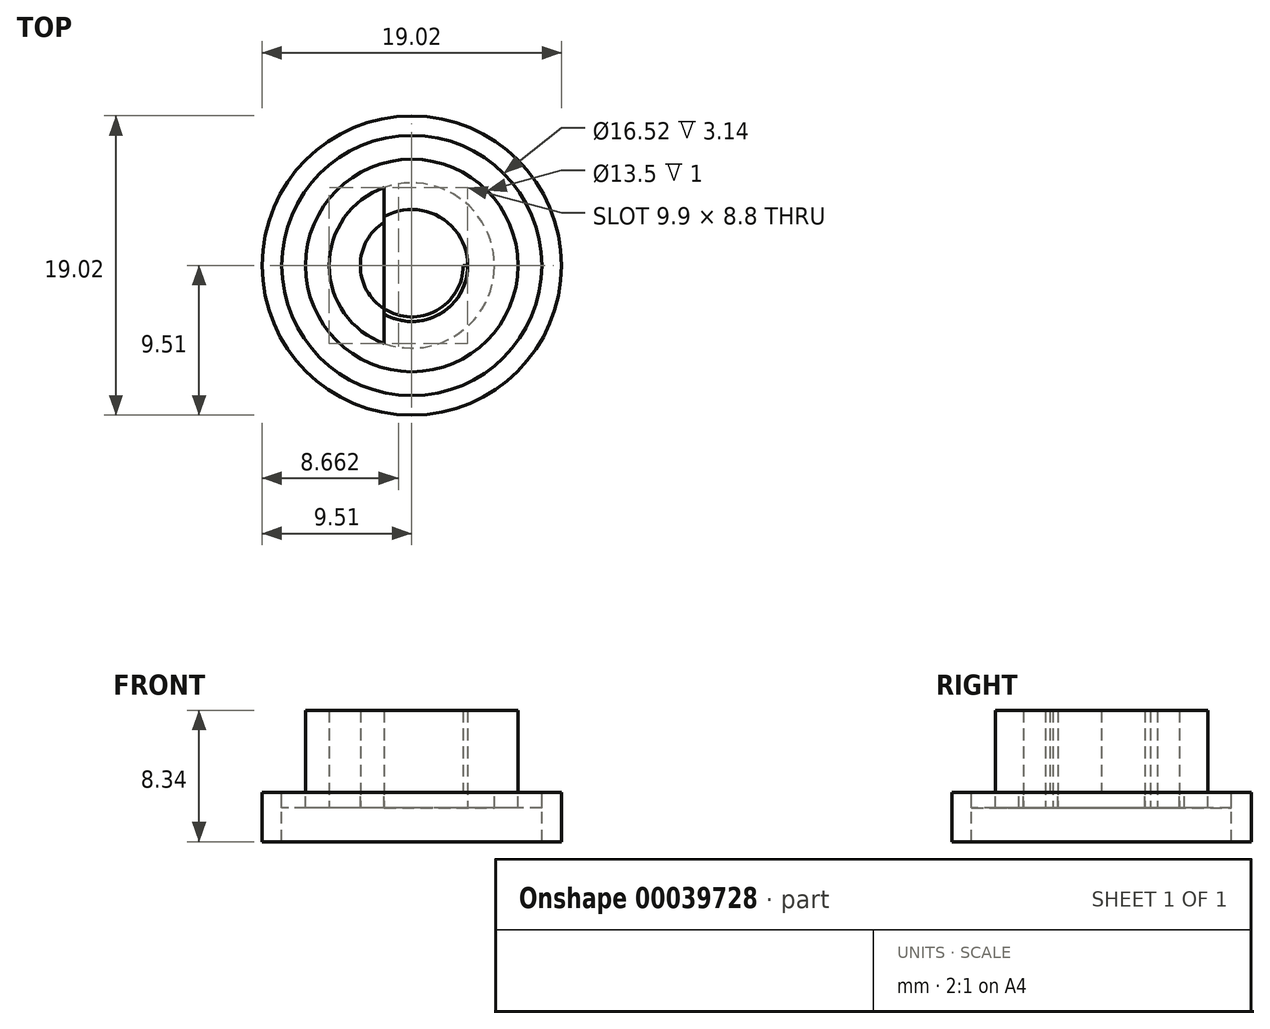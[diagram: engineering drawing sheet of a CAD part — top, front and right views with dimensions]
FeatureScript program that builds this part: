
annotation { "Feature Type Name" : "Feature", "Feature Type Description" : "" }
export const myFeature = defineFeature(function(context is Context, id is Id, definition is map)
    precondition{}
    {
        {
            var Q0;
            Q0=qCreatedBy(makeId("Top.planeOp"),FACE);
            var sketch = newSketch(context, id + "F0", { "sketchPlane" : qUnion([Q0])});
            skCircle(sketch, "E0", {"center": v(0, 0) * mm, "radius": 3.56 * mm});
            skCircle(sketch, "E1", {"center": v(0, 0) * mm, "radius": 5.25 * mm});
            skCircle(sketch, "E2", {"center": v(0, 0) * mm, "radius": 6.75 * mm});
            skLineSegment(sketch, "E3", {"start": v(3.56, 0) * mm, "end": v(-3.56, 0) * mm, "construction": true});
            skLineSegment(sketch, "E4", {"start": v(3.56, 0) * mm, "end": v(-1.74, 0) * mm});
            skLineSegment(sketch, "E5", {"start": v(-1.74, 4.95) * mm, "end": v(-1.74, -4.95) * mm});
            skCircle(sketch, "E6", {"center": v(0, 0) * mm, "radius": 8.26 * mm});
            skCircle(sketch, "E7", {"center": v(0, 0) * mm, "radius": 9.5 * mm});
            skCircle(sketch, "E8", {"center": v(0, 0) * mm, "radius": 2.48 * mm});
            skCircle(sketch, "E9", {"center": v(0, 0) * mm, "radius": 3.27 * mm});
            skSolve(sketch);
        }
        {
            var Q0;
            {var subQ1=sQuery(id+"F0.wireOp",EDGE,"E0");var subQ6=makeQuery(id+"F0.imprint","INTERSECT",VERTEX,{"derivedFrom":[subQ1,sQuery(id+"F0.wireOp",EDGE,"E4")]});Q0=makeQuery(id+"F0.imprint","IMPRINT",FACE,{"disambiguationData":[TD([[makeQuery(id+"F0.imprint","IMPRINT",EDGE,{"disambiguationData":[TD([[subQ6,-1.0]])],"derivedFrom":subQ1}),-1.0]])]});}
            extrude(context, id + "F1", {"entities" : qUnion([Q0]), "depth" : 3 * mm, "hasSecondDirection" : true, "secondDirectionOppositeDirection" : true, "secondDirectionDepth" : 1 * mm});
        }
        {
            var Q0;
            Q0=makeQuery(id+"F0.imprint","IMPRINT",FACE,{"disambiguationData":[TD([[makeQuery(id+"F0.imprint","IMPRINT",EDGE,{"derivedFrom":sQuery(id+"F0.wireOp",EDGE,"E2")}),1.0]])]});
            var Q1;
            {var subQ0=sQuery(id+"F0.wireOp",EDGE,"E5");var subQ1=sQuery(id+"F0.wireOp",EDGE,"E0");var subQ2=makeQuery(id+"F0.imprint","INTERSECT",VERTEX,{"disambiguationData":[OD(0.0)],"derivedFrom":[subQ1,subQ0]});Q1=makeQuery(id+"F0.imprint","IMPRINT",FACE,{"disambiguationData":[TD([[makeQuery(id+"F0.imprint","IMPRINT",EDGE,{"disambiguationData":[TD([[subQ2,-1.0]])],"derivedFrom":subQ1}),-1.0]])]});}
            extrude(context, id + "F2", {"entities" : qUnion([Q0, Q1]), "operationType" : NewBodyOperationType.ADD, "depth" : 5.2 * mm, "hasSecondDirection" : true, "secondDirectionOppositeDirection" : true, "secondDirectionDepth" : 1 * mm});
        }
        {
            var Q0;
            Q0=makeQuery(id+"F0.imprint","IMPRINT",FACE,{"disambiguationData":[TD([[makeQuery(id+"F0.imprint","IMPRINT",EDGE,{"derivedFrom":sQuery(id+"F0.wireOp",EDGE,"E2")}),-1.0]])]});
            var Q1;
            {var subQ1=sQuery(id+"F0.wireOp",EDGE,"E5");var subQ3=sQuery(id+"F0.wireOp",EDGE,"E4");var subQ5=makeQuery(id+"F0.imprint","INTERSECT",VERTEX,{"derivedFrom":[subQ3,subQ1]});Q1=makeQuery(id+"F0.imprint","IMPRINT",FACE,{"disambiguationData":[TD([[makeQuery(id+"F0.imprint","IMPRINT",EDGE,{"disambiguationData":[TD([[subQ5,1.0]])],"derivedFrom":subQ3}),-1.0]])]});}
            var Q2;
            {var subQ3=sQuery(id+"F0.wireOp",EDGE,"E0");var subQ5=sQuery(id+"F0.wireOp",EDGE,"E4");var subQ7=makeQuery(id+"F0.imprint","INTERSECT",VERTEX,{"derivedFrom":[subQ3,subQ5]});Q2=makeQuery(id+"F0.imprint","IMPRINT",FACE,{"disambiguationData":[TD([[makeQuery(id+"F0.imprint","IMPRINT",EDGE,{"disambiguationData":[TD([[subQ7,-1.0]])],"derivedFrom":subQ3}),1.0]])]});}
            var Q3;
            {var subQ1=sQuery(id+"F0.wireOp",EDGE,"E5");var subQ3=sQuery(id+"F0.wireOp",EDGE,"E4");var subQ5=makeQuery(id+"F0.imprint","INTERSECT",VERTEX,{"derivedFrom":[subQ3,subQ1]});Q3=makeQuery(id+"F0.imprint","IMPRINT",FACE,{"disambiguationData":[TD([[makeQuery(id+"F0.imprint","IMPRINT",EDGE,{"disambiguationData":[TD([[subQ5,1.0]])],"derivedFrom":subQ3}),1.0]])]});}
            var Q4;
            {var subQ0=sQuery(id+"F0.wireOp",EDGE,"E9");var subQ3=sQuery(id+"F0.wireOp",EDGE,"E4");var subQ4=makeQuery(id+"F0.imprint","INTERSECT",VERTEX,{"derivedFrom":[subQ3,subQ0]});Q4=makeQuery(id+"F0.imprint","IMPRINT",FACE,{"disambiguationData":[TD([[makeQuery(id+"F0.imprint","IMPRINT",EDGE,{"disambiguationData":[TD([[subQ4,-1.0]])],"derivedFrom":subQ3}),1.0]])]});}
            var Q5;
            {var subQ1=sQuery(id+"F0.wireOp",EDGE,"E5");var subQ4=makeQuery(id+"F0.imprint","INTERSECT",VERTEX,{"derivedFrom":[sQuery(id+"F0.wireOp",EDGE,"E4"),subQ1]});Q5=makeQuery(id+"F0.imprint","IMPRINT",FACE,{"disambiguationData":[TD([[makeQuery(id+"F0.imprint","IMPRINT",EDGE,{"disambiguationData":[TD([[subQ4,1.0]])],"derivedFrom":subQ1}),-1.0]])]});}
            var Q6;
            {var subQ0=sQuery(id+"F0.wireOp",EDGE,"E9");var subQ1=sQuery(id+"F0.wireOp",EDGE,"E5");var subQ3=makeQuery(id+"F0.imprint","INTERSECT",VERTEX,{"disambiguationData":[OD(0.0)],"derivedFrom":[subQ1,subQ0]});Q6=makeQuery(id+"F0.imprint","IMPRINT",FACE,{"disambiguationData":[TD([[makeQuery(id+"F0.imprint","IMPRINT",EDGE,{"disambiguationData":[TD([[subQ3,-1.0]])],"derivedFrom":subQ1}),-1.0]])]});}
            var Q7;
            {var subQ3=sQuery(id+"F0.wireOp",EDGE,"E4");var subQ5=sQuery(id+"F0.wireOp",EDGE,"E0");var subQ7=makeQuery(id+"F0.imprint","INTERSECT",VERTEX,{"derivedFrom":[subQ5,subQ3]});Q7=makeQuery(id+"F0.imprint","IMPRINT",FACE,{"disambiguationData":[TD([[makeQuery(id+"F0.imprint","IMPRINT",EDGE,{"disambiguationData":[TD([[subQ7,1.0]])],"derivedFrom":subQ5}),1.0]])]});}
            var Q8;
            {var subQ3=sQuery(id+"F0.wireOp",EDGE,"E9");var subQ5=sQuery(id+"F0.wireOp",EDGE,"E4");var subQ6=makeQuery(id+"F0.imprint","INTERSECT",VERTEX,{"derivedFrom":[subQ5,subQ3]});Q8=makeQuery(id+"F0.imprint","IMPRINT",FACE,{"disambiguationData":[TD([[makeQuery(id+"F0.imprint","IMPRINT",EDGE,{"disambiguationData":[TD([[subQ6,-1.0]])],"derivedFrom":subQ5}),-1.0]])]});}
            var Q9;
            {var subQ0=sQuery(id+"F0.wireOp",EDGE,"E5");var subQ1=sQuery(id+"F0.wireOp",EDGE,"E0");var subQ2=makeQuery(id+"F0.imprint","INTERSECT",VERTEX,{"disambiguationData":[OD(0.0)],"derivedFrom":[subQ1,subQ0]});Q9=makeQuery(id+"F0.imprint","IMPRINT",FACE,{"disambiguationData":[TD([[makeQuery(id+"F0.imprint","IMPRINT",EDGE,{"disambiguationData":[TD([[subQ2,-1.0]])],"derivedFrom":subQ1}),-1.0]])]});}
            var Q10;
            {var subQ0=sQuery(id+"F0.wireOp",EDGE,"E5");var subQ3=sQuery(id+"F0.wireOp",EDGE,"E0");var subQ6=makeQuery(id+"F0.imprint","INTERSECT",VERTEX,{"disambiguationData":[OD(0.0)],"derivedFrom":[subQ3,subQ0]});Q10=makeQuery(id+"F0.imprint","IMPRINT",FACE,{"disambiguationData":[TD([[makeQuery(id+"F0.imprint","IMPRINT",EDGE,{"disambiguationData":[TD([[subQ6,-1.0]])],"derivedFrom":subQ3}),1.0]])]});}
            extrude(context, id + "F3", {"entities" : qUnion([Q0, Q1, Q2, Q3, Q4, Q5, Q6, Q7, Q8, Q9, Q10]), "oppositeDirection" : true, "depth" : 1 * mm});
        }
        {
            var Q0;
            Q0=makeQuery(id+"F0.imprint","IMPRINT",FACE,{"disambiguationData":[TD([[makeQuery(id+"F0.imprint","IMPRINT",EDGE,{"derivedFrom":sQuery(id+"F0.wireOp",EDGE,"E6")}),-1.0]])]});
            extrude(context, id + "F4", {"entities" : qUnion([Q0]), "oppositeDirection" : true, "depth" : 3.14 * mm});
        }
        {
            var Q0;
            {var subQ0=sQuery(id+"F0.wireOp",EDGE,"E5");var subQ3=sQuery(id+"F0.wireOp",EDGE,"E0");var subQ6=makeQuery(id+"F0.imprint","INTERSECT",VERTEX,{"disambiguationData":[OD(0.0)],"derivedFrom":[subQ3,subQ0]});Q0=makeQuery(id+"F0.imprint","IMPRINT",FACE,{"disambiguationData":[TD([[makeQuery(id+"F0.imprint","IMPRINT",EDGE,{"disambiguationData":[TD([[subQ6,-1.0]])],"derivedFrom":subQ3}),1.0]])]});}
            extrude(context, id + "F5", {"entities" : qUnion([Q0]), "depth" : 5.2 * mm});
        }
        {
            var Q0;
            {var subQ0=sQuery(id+"F0.wireOp",EDGE,"E9");var subQ1=sQuery(id+"F0.wireOp",EDGE,"E5");var subQ3=makeQuery(id+"F0.imprint","INTERSECT",VERTEX,{"disambiguationData":[OD(0.0)],"derivedFrom":[subQ1,subQ0]});Q0=makeQuery(id+"F0.imprint","IMPRINT",FACE,{"disambiguationData":[TD([[makeQuery(id+"F0.imprint","IMPRINT",EDGE,{"disambiguationData":[TD([[subQ3,-1.0]])],"derivedFrom":subQ1}),-1.0]])]});}
            var Q1;
            {var subQ1=sQuery(id+"F0.wireOp",EDGE,"E5");var subQ4=makeQuery(id+"F0.imprint","INTERSECT",VERTEX,{"derivedFrom":[sQuery(id+"F0.wireOp",EDGE,"E4"),subQ1]});Q1=makeQuery(id+"F0.imprint","IMPRINT",FACE,{"disambiguationData":[TD([[makeQuery(id+"F0.imprint","IMPRINT",EDGE,{"disambiguationData":[TD([[subQ4,1.0]])],"derivedFrom":subQ1}),-1.0]])]});}
            extrude(context, id + "F6", {"entities" : qUnion([Q0, Q1]), "depth" : 5.2 * mm, "hasSecondDirection" : true, "secondDirectionOppositeDirection" : true, "secondDirectionDepth" : 1 * mm});
        }
    });
